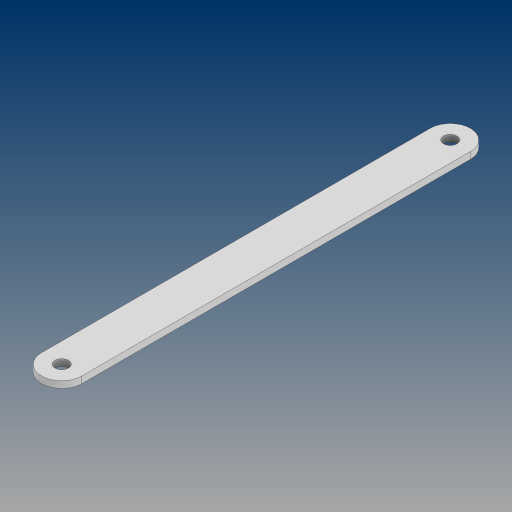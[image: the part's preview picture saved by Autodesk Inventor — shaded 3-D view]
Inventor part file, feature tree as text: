
AUTODESK INVENTOR PART (.ipt)
format: ipt  version: 2024.3 (Build 283343000, 343)  size: 97,280 bytes
history: native  units: in
note: dims shown in document units (in); Inventor stores cm internally (conversion verified against a paired STEP export)
features: extrude x1, sketch x1
ambient origin geometry x8: Origin, YZ Plane, XZ Plane, XY Plane, X Axis, Y Axis, Z Axis, Center Point
bodies: Solid1 (feature_tree)
feature tree (2):
  extrude  "Extrusion1"  Depth=0.25in
  sketch  "Sketch1"  dims[d0=14.5in d1=0.5in d2=0.5in d3=0.5in d4=0.5in d5=0.25in d6=0.0in]
